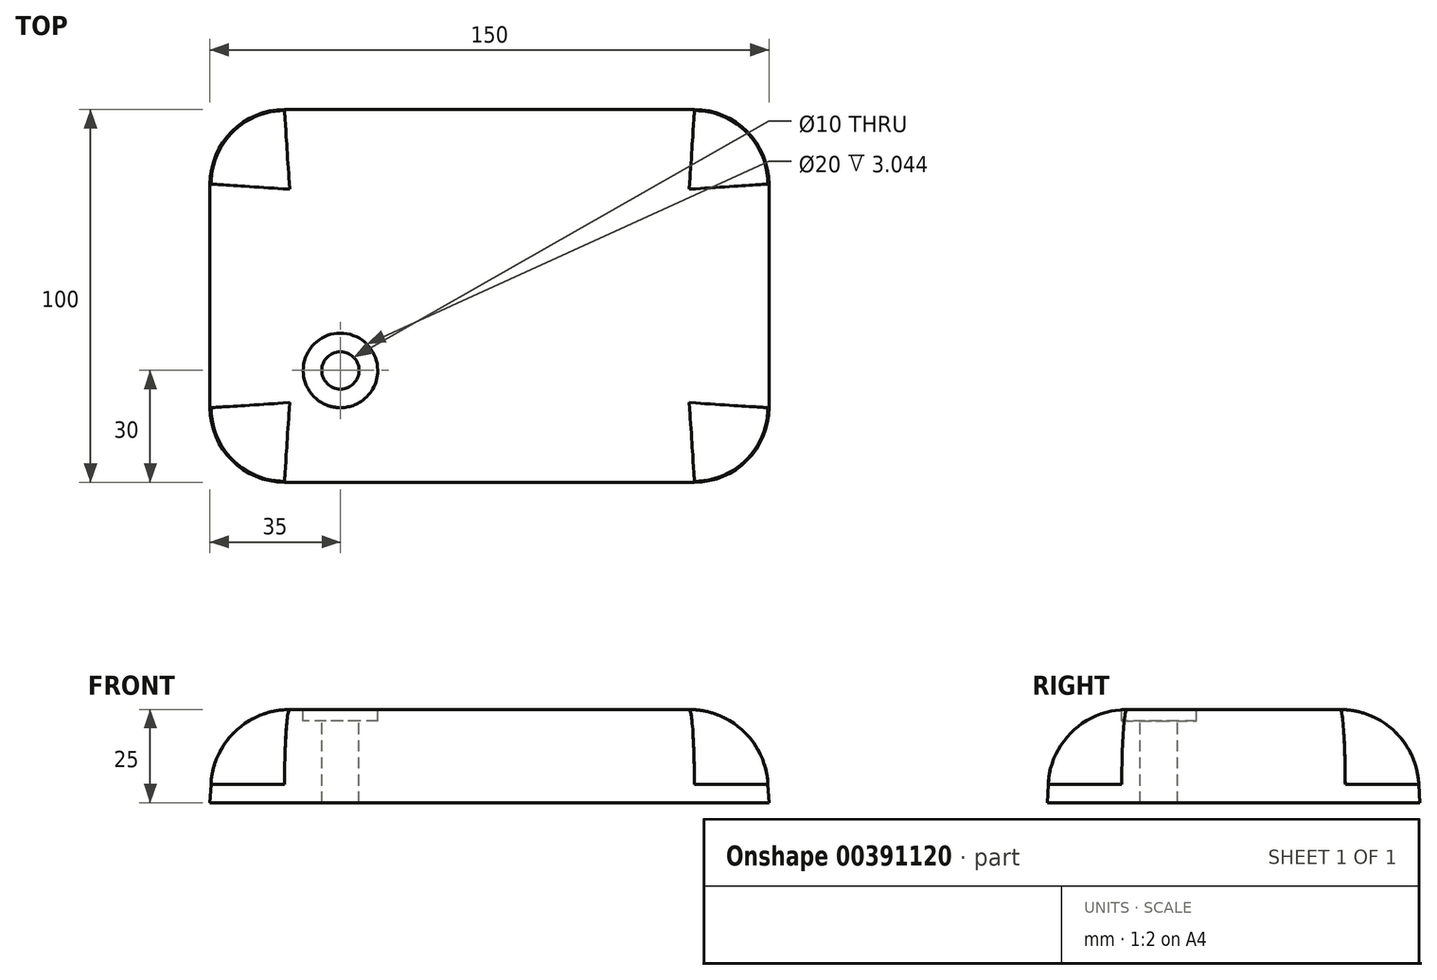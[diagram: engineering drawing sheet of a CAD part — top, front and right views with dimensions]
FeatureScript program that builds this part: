
annotation { "Feature Type Name" : "Feature", "Feature Type Description" : "" }
export const myFeature = defineFeature(function(context is Context, id is Id, definition is map)
    precondition{}
    {
        {
            var Q0;
            Q0=qCreatedBy(makeId("Top.planeOp"),FACE);
            var sketch = newSketch(context, id + "F0", { "sketchPlane" : qUnion([Q0])});
            skLineSegment(sketch, "E0.bottom", {"start": v(55, -50) * mm, "end": v(-55, -50) * mm});
            skLineSegment(sketch, "E0.top", {"start": v(55, 50) * mm, "end": v(-55, 50) * mm});
            skLineSegment(sketch, "E0.left", {"start": v(75, -30) * mm, "end": v(75, 30) * mm});
            skLineSegment(sketch, "E0.right", {"start": v(-75, -30) * mm, "end": v(-75, 30) * mm});
            skPoint(sketch, "E0.middle", {"position": v(0, 0) * mm});
            skPoint(sketch, "E1.visualSharp", {"position": v(-75, -50) * mm});
            skArc(sketch, "E1.filletArc", {"start": v(-75, -30) * mm, "mid": v(-69.14, -44.14) * mm, "end": v(-55, -50) * mm});
            skPoint(sketch, "E2.visualSharp", {"position": v(-75, 50) * mm});
            skArc(sketch, "E2.filletArc", {"start": v(-55, 50) * mm, "mid": v(-69.14, 44.14) * mm, "end": v(-75, 30) * mm});
            skPoint(sketch, "E3.visualSharp", {"position": v(75, 50) * mm});
            skArc(sketch, "E3.filletArc", {"start": v(75, 30) * mm, "mid": v(69.14, 44.14) * mm, "end": v(55, 50) * mm});
            skPoint(sketch, "E4.visualSharp", {"position": v(75, -50) * mm});
            skArc(sketch, "E4.filletArc", {"start": v(55, -50) * mm, "mid": v(69.14, -44.14) * mm, "end": v(75, -30) * mm});
            skSolve(sketch);
        }
        {
            var Q0;
            Q0 = qSketchRegion(id + "F0", true);
            extrude(context, id + "F1", {"entities" : qUnion([Q0]), "depth" : 25 * mm, "hasDraft" : true, "draftAngle" : 3 * degree, "draftPullDirection" : true});
        }
        {
            var Q0;
            Q0=makeQuery(id+"F1.opExtrude","CAP_EDGE",EDGE,{"disambiguationData":[OSD([sQuery(id+"F0.wireOp",EDGE,"E0.bottom")])],"isStart":false});
            fillet(context, id + "F2", {"entities" : qUnion([Q0]), "radius" : 21.13 * mm, "tangentPropagation" : true, "allowEdgeOverflow" : false});
        }
        {
            var Q0;
            Q0=makeQuery(id+"F1.opExtrude","CAP_FACE",FACE,{"disambiguationData":[OSD([sQuery(id+"F0.wireOp",EDGE,"E0.bottom"),sQuery(id+"F0.wireOp",EDGE,"E0.top"),sQuery(id+"F0.wireOp",EDGE,"E0.left"),sQuery(id+"F0.wireOp",EDGE,"E0.right"),sQuery(id+"F0.wireOp",EDGE,"E1.filletArc"),sQuery(id+"F0.wireOp",EDGE,"E2.filletArc"),sQuery(id+"F0.wireOp",EDGE,"E3.filletArc"),sQuery(id+"F0.wireOp",EDGE,"E4.filletArc")])],"isStart":false});
            var sketch = newSketch(context, id + "F3", { "sketchPlane" : qUnion([Q0])});
            skPoint(sketch, "E5", {"position": v(-40, -20) * mm});
            skSolve(sketch);
        }
        {
            var Q0;
            Q0=sQuery(id+"F3.wireOp",VERTEX,"E5");
            var Q1;
            Q1=makeQuery(id+"F1.opExtrude","SWEPT_BODY",BODY,{"disambiguationData":[OSD([sQuery(id+"F0.wireOp",EDGE,"E0.bottom"),sQuery(id+"F0.wireOp",EDGE,"E0.top"),sQuery(id+"F0.wireOp",EDGE,"E0.left"),sQuery(id+"F0.wireOp",EDGE,"E0.right"),sQuery(id+"F0.wireOp",EDGE,"E1.filletArc"),sQuery(id+"F0.wireOp",EDGE,"E2.filletArc"),sQuery(id+"F0.wireOp",EDGE,"E3.filletArc"),sQuery(id+"F0.wireOp",EDGE,"E4.filletArc")])]});
            hole(context, id + "F4", {"style" : HoleStyle.C_BORE, "endStyle" : HoleEndStyle.THROUGH, "holeDiameter" : 10 * mm, "cBoreDiameter" : 20 * mm, "cBoreDepth" : 3 * mm, "isTappedThrough" : true, "tappedDepth" : 12 * mm, "tapClearance" : 3, "locations" : qUnion([Q0]), "scope" : qUnion([Q1])});
        }
    });
